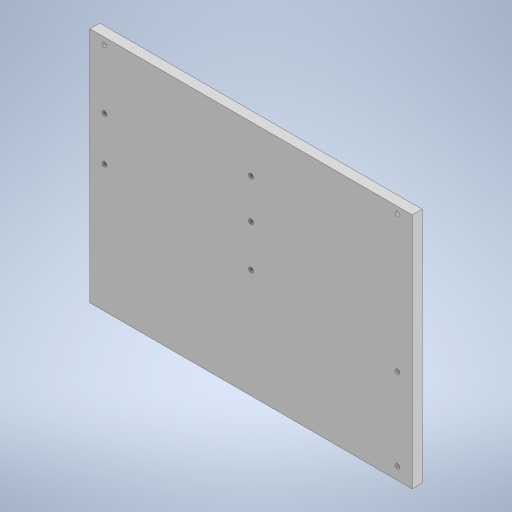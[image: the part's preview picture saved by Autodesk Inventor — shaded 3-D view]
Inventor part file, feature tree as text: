
AUTODESK INVENTOR PART (.ipt)
format: ipt  version: 2023 (Build 270158000, 158)  size: 229,888 bytes
history: native  units: mm
features: extrude x2, sketch x2
ambient origin geometry x8: Origin, YZ Plane, XZ Plane, XY Plane, X Axis, Y Axis, Z Axis, Center Point
bodies: Solide1 (feature_tree)
feature tree (4):
  extrude  "Extrusion1"  Depth=220.0mm
  extrude  "Extrusion2"  Depth=162.0mm
  sketch  "Esquisse1"
  sketch  "Esquisse2"
